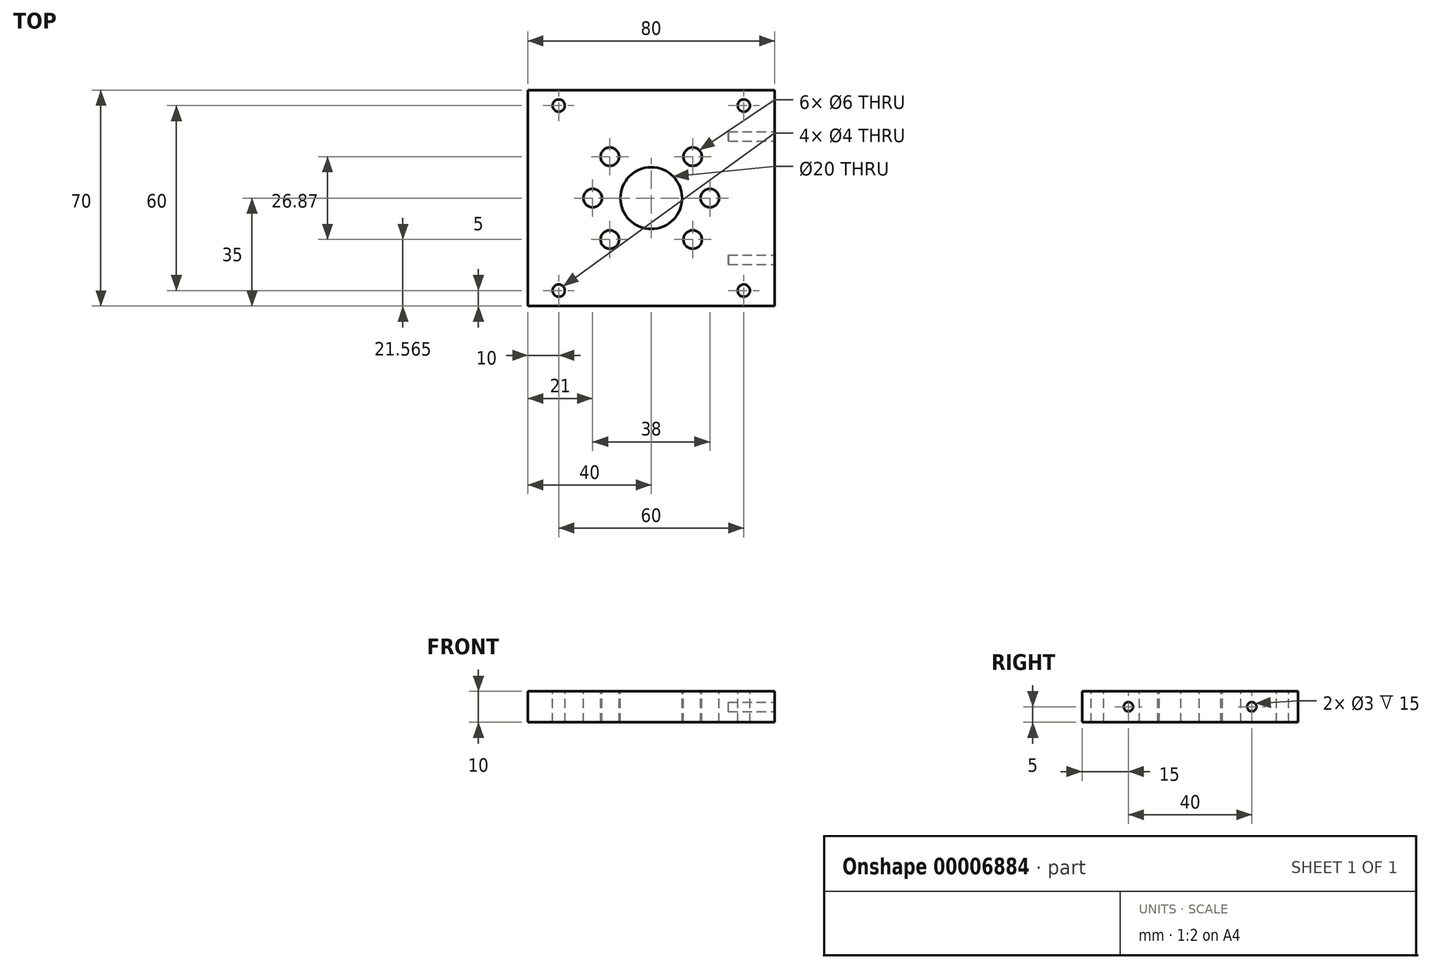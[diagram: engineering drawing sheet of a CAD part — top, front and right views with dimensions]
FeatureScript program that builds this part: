
annotation { "Feature Type Name" : "Feature", "Feature Type Description" : "" }
export const myFeature = defineFeature(function(context is Context, id is Id, definition is map)
    precondition{}
    {
        {
            var Q0;
            Q0=qCreatedBy(makeId("Top.planeOp"),FACE);
            var sketch = newSketch(context, id + "F0", { "sketchPlane" : qUnion([Q0])});
            skLineSegment(sketch, "E0.rect.bottom", {"start": v(40, -35) * mm, "end": v(-40, -35) * mm});
            skLineSegment(sketch, "E0.rect.top", {"start": v(40, 35) * mm, "end": v(-40, 35) * mm});
            skLineSegment(sketch, "E0.rect.left", {"start": v(40, -35) * mm, "end": v(40, 35) * mm});
            skLineSegment(sketch, "E0.rect.right", {"start": v(-40, -35) * mm, "end": v(-40, 35) * mm});
            skPoint(sketch, "E0.rect.middle", {"position": v(0, 0) * mm});
            skSolve(sketch);
        }
        {
            var Q0;
            {var subQ1=sQuery(id+"F0.wireOp",EDGE,"E0.rect.left");Q0=makeQuery(id+"F0.imprint","IMPRINT",FACE,{"disambiguationData":[TD([[makeQuery(id+"F0.imprint","IMPRINT",EDGE,{"derivedFrom":subQ1}),1.0]])]});}
            var Q1;
            {var subQ1=sQuery(id+"F0.wireOp",EDGE,"E0.rect.right");Q1=makeQuery(id+"F0.imprint","IMPRINT",FACE,{"disambiguationData":[TD([[makeQuery(id+"F0.imprint","IMPRINT",EDGE,{"derivedFrom":subQ1}),-1.0]])]});}
            extrude(context, id + "F1", {"entities" : qUnion([Q0, Q1]), "depth" : 10 * mm});
        }
        {
            var Q0;
            Q0=makeQuery(id+"F1.opExtrude","CAP_FACE",FACE,{"disambiguationData":[OSD([sQuery(id+"F0.wireOp",EDGE,"E0.rect.bottom"),sQuery(id+"F0.wireOp",EDGE,"E0.rect.top"),sQuery(id+"F0.wireOp",EDGE,"E0.rect.left"),sQuery(id+"F0.wireOp",EDGE,"E0.rect.right")])],"isStart":false});
            var sketch = newSketch(context, id + "F2", { "sketchPlane" : qUnion([Q0])});
            skLineSegment(sketch, "E1", {"start": v(0, 35) * mm, "end": v(0, -35) * mm, "construction": true});
            skLineSegment(sketch, "E2", {"start": v(20, 0) * mm, "end": v(-40, 0) * mm, "construction": true});
            skCircle(sketch, "E3", {"center": v(0, 0) * mm, "radius": 10 * mm});
            skCircle(sketch, "E4", {"center": v(0, 0) * mm, "radius": 19 * mm, "construction": true});
            skCircle(sketch, "E5", {"center": v(-19, 0) * mm, "radius": 3 * mm});
            skCircle(sketch, "E6", {"center": v(19, 0) * mm, "radius": 3 * mm});
            skLineSegment(sketch, "E7", {"start": v(0, 0) * mm, "end": v(-19.33, 19.33) * mm, "construction": true});
            skLineSegment(sketch, "E8", {"start": v(0, 0) * mm, "end": v(-18.3, -18.3) * mm, "construction": true});
            skLineSegment(sketch, "E9", {"start": v(0, 0) * mm, "end": v(16.8, 16.8) * mm, "construction": true});
            skLineSegment(sketch, "E10", {"start": v(0, 0) * mm, "end": v(17.78, -17.78) * mm, "construction": true});
            skCircle(sketch, "E11", {"center": v(-13.44, 13.44) * mm, "radius": 3 * mm});
            skCircle(sketch, "E12", {"center": v(-13.44, -13.44) * mm, "radius": 3 * mm});
            skCircle(sketch, "E13", {"center": v(13.44, -13.44) * mm, "radius": 3 * mm});
            skCircle(sketch, "E14", {"center": v(13.44, 13.44) * mm, "radius": 3 * mm});
            skSolve(sketch);
        }
        {
            var Q0;
            Q0=makeQuery(id+"F2.imprint","IMPRINT",FACE,{"disambiguationData":[TD([[makeQuery(id+"F2.imprint","IMPRINT",EDGE,{"derivedFrom":sQuery(id+"F2.wireOp",EDGE,"E3")}),1.0]])]});
            var Q1;
            Q1=makeQuery(id+"F2.imprint","IMPRINT",FACE,{"disambiguationData":[TD([[makeQuery(id+"F2.imprint","IMPRINT",EDGE,{"derivedFrom":sQuery(id+"F2.wireOp",EDGE,"E5")}),1.0]])]});
            var Q2;
            Q2=makeQuery(id+"F2.imprint","IMPRINT",FACE,{"disambiguationData":[TD([[makeQuery(id+"F2.imprint","IMPRINT",EDGE,{"derivedFrom":sQuery(id+"F2.wireOp",EDGE,"E6")}),1.0]])]});
            var Q3;
            Q3=makeQuery(id+"F2.imprint","IMPRINT",FACE,{"disambiguationData":[TD([[makeQuery(id+"F2.imprint","IMPRINT",EDGE,{"derivedFrom":sQuery(id+"F2.wireOp",EDGE,"E12")}),1.0]])]});
            var Q4;
            Q4=makeQuery(id+"F2.imprint","IMPRINT",FACE,{"disambiguationData":[TD([[makeQuery(id+"F2.imprint","IMPRINT",EDGE,{"derivedFrom":sQuery(id+"F2.wireOp",EDGE,"E13")}),1.0]])]});
            var Q5;
            Q5=makeQuery(id+"F2.imprint","IMPRINT",FACE,{"disambiguationData":[TD([[makeQuery(id+"F2.imprint","IMPRINT",EDGE,{"derivedFrom":sQuery(id+"F2.wireOp",EDGE,"E14")}),1.0]])]});
            var Q6;
            Q6=makeQuery(id+"F2.imprint","IMPRINT",FACE,{"disambiguationData":[TD([[makeQuery(id+"F2.imprint","IMPRINT",EDGE,{"derivedFrom":sQuery(id+"F2.wireOp",EDGE,"E11")}),1.0]])]});
            extrude(context, id + "F3", {"entities" : qUnion([Q0, Q1, Q2, Q3, Q4, Q5, Q6]), "operationType" : NewBodyOperationType.REMOVE, "oppositeDirection" : true, "depth" : 25 * mm});
        }
        {
            var Q0;
            Q0=makeQuery(id+"F1.opExtrude","CAP_FACE",FACE,{"disambiguationData":[OSD([sQuery(id+"F0.wireOp",EDGE,"E0.rect.bottom"),sQuery(id+"F0.wireOp",EDGE,"E0.rect.top"),sQuery(id+"F0.wireOp",EDGE,"E0.rect.left"),sQuery(id+"F0.wireOp",EDGE,"E0.rect.right")])],"isStart":false});
            var sketch = newSketch(context, id + "F4", { "sketchPlane" : qUnion([Q0])});
            skLineSegment(sketch, "E15", {"start": v(-40, 30) * mm, "end": v(40, 30) * mm, "construction": true});
            skLineSegment(sketch, "E16", {"start": v(-40, -30) * mm, "end": v(40, -30) * mm, "construction": true});
            skCircle(sketch, "E17", {"center": v(-30, 30) * mm, "radius": 2 * mm});
            skCircle(sketch, "E18", {"center": v(30, 30) * mm, "radius": 2 * mm});
            skCircle(sketch, "E19", {"center": v(30, -30) * mm, "radius": 2 * mm});
            skCircle(sketch, "E20", {"center": v(-30, -30) * mm, "radius": 2 * mm});
            skSolve(sketch);
        }
        {
            var Q0;
            Q0 = qSketchRegion(id + "F4", true);
            extrude(context, id + "F5", {"entities" : qUnion([Q0]), "operationType" : NewBodyOperationType.REMOVE, "endBound" : BoundingType.THROUGH_ALL, "oppositeDirection" : true, "depth" : 25 * mm});
        }
        {
            var Q0;
            Q0=makeQuery(id+"F1.opExtrude","SWEPT_FACE",FACE,{"disambiguationData":[OSD([sQuery(id+"F0.wireOp",EDGE,"E0.rect.left")])]});
            var sketch = newSketch(context, id + "F6", { "sketchPlane" : qUnion([Q0])});
            skLineSegment(sketch, "E21", {"start": v(-35, 5) * mm, "end": v(35, 5) * mm, "construction": true});
            skCircle(sketch, "E22", {"center": v(-20, 5) * mm, "radius": 1.5 * mm});
            skCircle(sketch, "E23", {"center": v(20, 5) * mm, "radius": 1.5 * mm});
            skSolve(sketch);
        }
        {
            var Q0;
            Q0 = qSketchRegion(id + "F6", true);
            extrude(context, id + "F7", {"entities" : qUnion([Q0]), "operationType" : NewBodyOperationType.REMOVE, "oppositeDirection" : true, "depth" : (15) * mm});
        }
    });
